# Revit family: 0005725
name_source: partatom
category: Lighting Fixtures
revit_build: Autodesk Revit 2017 (Build: 20190507_1515(x64)
units: mm (PartAtom-declared; Revit-internal decimal feet)

## family parameters
Cut with Voids When Loaded = No
Host = Face
Light Source = No
OmniClass Number = 23.80.70.00
OmniClass Title = Lighting
Part Type = Normal
Room Calculation Point = No
Round Connector Dimension = Use Diameter
Shared = No

## types (1)
- 0005725 Sylspot Kit R 345LM 830 ADJ IP20 WH
    Apparent Load = 5 VA
    Assembly Code = D5020200
    AssetType = Fixed
    AxisFromBottom_SYL = 7 mm  [stored 0.0229659 ft]
    ClassificationName = Uniclass2015
    ClassificationValue = EF_70_80
    Cost = 0 $
    Default Elevation = 1219 mm
    Description = Recessed spotlight Kit with RefLED GU10 LED spotlight lamp Ø50mm. Polycarbonate body, round bezel ring in white color finish, vertical tilt 25°, IP20 degree of protection, class II. Lumen output 345lm, CCT 3000K, beam angle 36°, power 4,5W, efficacy 77 lm/W, lifetime 15.000h. Outer dimensions: Ø80x90mm, cut-out Ø68-76mm. Suitable for internal environment only and for LED lamps only.
    DocumentationLiterature = http://www.sylvania-lighting.com
    ElectricShockClassification = Class II
    HeightHousing_SYL = 32 mm
    IfcExportAs = IfcLightFixtureType
    IfcExportType = IfcLightFixtureType
    ImpactProtectionIndex = IK02
    IngressProtection = IP20
    InputNominalFrequency = 50/60 Hz
    InputVoltage = 220-240 V AC
    Keynote = 16500
    Lamp = LED
    LampColourRenderingIndex = 80
    LampColourTemperature = 3000 K
    LampMacAdamStep = 6
    LampNominalLuminous = 345 lm
    LampsType = LED
    LuminousEfficacy = 77 lm/W
    Manufacturer = Feilo Sylvania
    ManufacturerName = Feilo Sylvania
    Material = pc polycarbonate housing
    Material_1_SYL = PC/ABS Plastic
    Material_2_SYL = LED
    Material_3_SYL = <By Category>
    Material_4_SYL = <By Category>
    Model = Sylspot Kit R 345lm 830 Adj IP20 WHT
    ModelNumber = 0005725
    ModelReference = Sylspot Kit R 345lm 830 Adj IP20 WHT
    Name = Sylspot Kit R 345lm 830 Adj IP20 WHT
    NominalDepth = 90 mm  [stored 0.295276 ft]
    NominalHeight = 85 mm  [stored 0.278871 ft]
    NominalLength = 90 mm  [stored 0.295276 ft]
    PowerConsumption = 4.5 W
    PowerFactor = 0
    RadiusCutOut_SYL = 35 mm  [stored 0.114829 ft]
    RadiusHousingUpper_SYL = 34 mm
    RadiusInner2_SYL = 29 mm  [stored 0.0951444 ft]
    Radius_SYL = 43 mm
    TrimHeight_SYL = 3 mm  [stored 0.00984252 ft]
    Type Image = <None>
    TypeLamp_SYL = SylSpot GU10 : 0005725 Sylspot Kit R 345LM 830 ADJ IP20 WH
    TypeName = Sylspot Kit R 345lm 830 Adj IP20 WHT
    URL = http://www.sylvania-lighting.com
    Voltage = 230 V
    Weight = 4.32 kg

note: [stored X ft] marks values corroborated as IEEE doubles in the binary element streams (Revit-internal decimal feet)

## geometry (parser evidence)
native form markers: Sweep x7
no freeform markers — native parametric forms only
